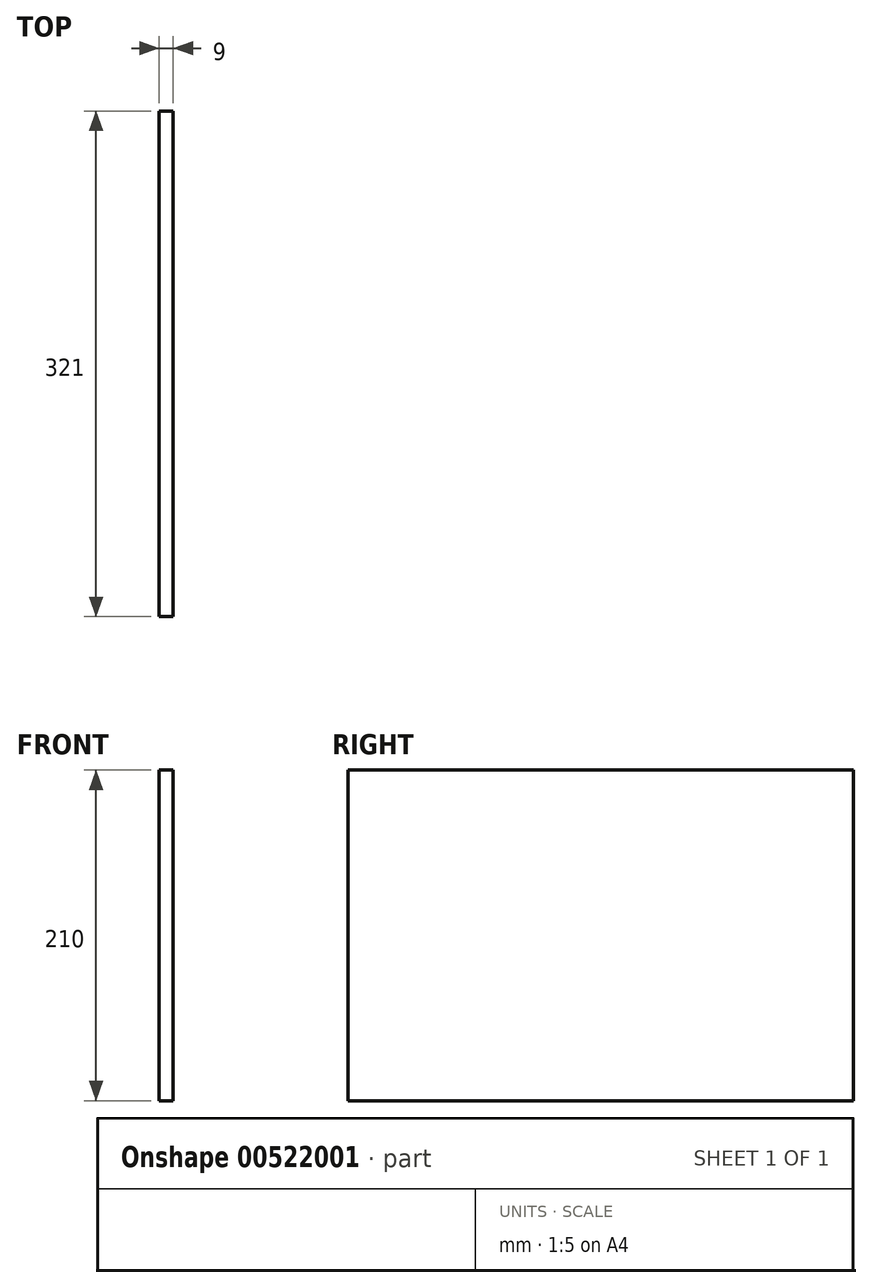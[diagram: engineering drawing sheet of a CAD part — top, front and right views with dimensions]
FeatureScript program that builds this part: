
annotation { "Feature Type Name" : "Feature", "Feature Type Description" : "" }
export const myFeature = defineFeature(function(context is Context, id is Id, definition is map)
    precondition{}
    {
        {
            var Q0;
            Q0=qCreatedBy(makeId("Right.planeOp"),FACE);
            var sketch = newSketch(context, id + "F0", { "sketchPlane" : qUnion([Q0])});
            skLineSegment(sketch, "E0.bottom", {"start": v(0, 0) * mm, "end": v(-321, 0) * mm});
            skLineSegment(sketch, "E0.top", {"start": v(0, 210) * mm, "end": v(-321, 210) * mm});
            skLineSegment(sketch, "E0.left", {"start": v(0, 0) * mm, "end": v(0, 210) * mm});
            skLineSegment(sketch, "E0.right", {"start": v(-321, 0) * mm, "end": v(-321, 210) * mm});
            skSolve(sketch);
        }
        {
            var Q0;
            Q0=makeQuery(id+"F0.imprint","IMPRINT",FACE,{"disambiguationData":[TD([[makeQuery(id+"F0.imprint","IMPRINT",EDGE,{"derivedFrom":sQuery(id+"F0.wireOp",EDGE,"E0.bottom")}),-1.0]])]});
            extrude(context, id + "F1", {"entities" : qUnion([Q0]), "depth" : 9 * mm, "offsetDistance" : 25 * mm});
        }
    });
